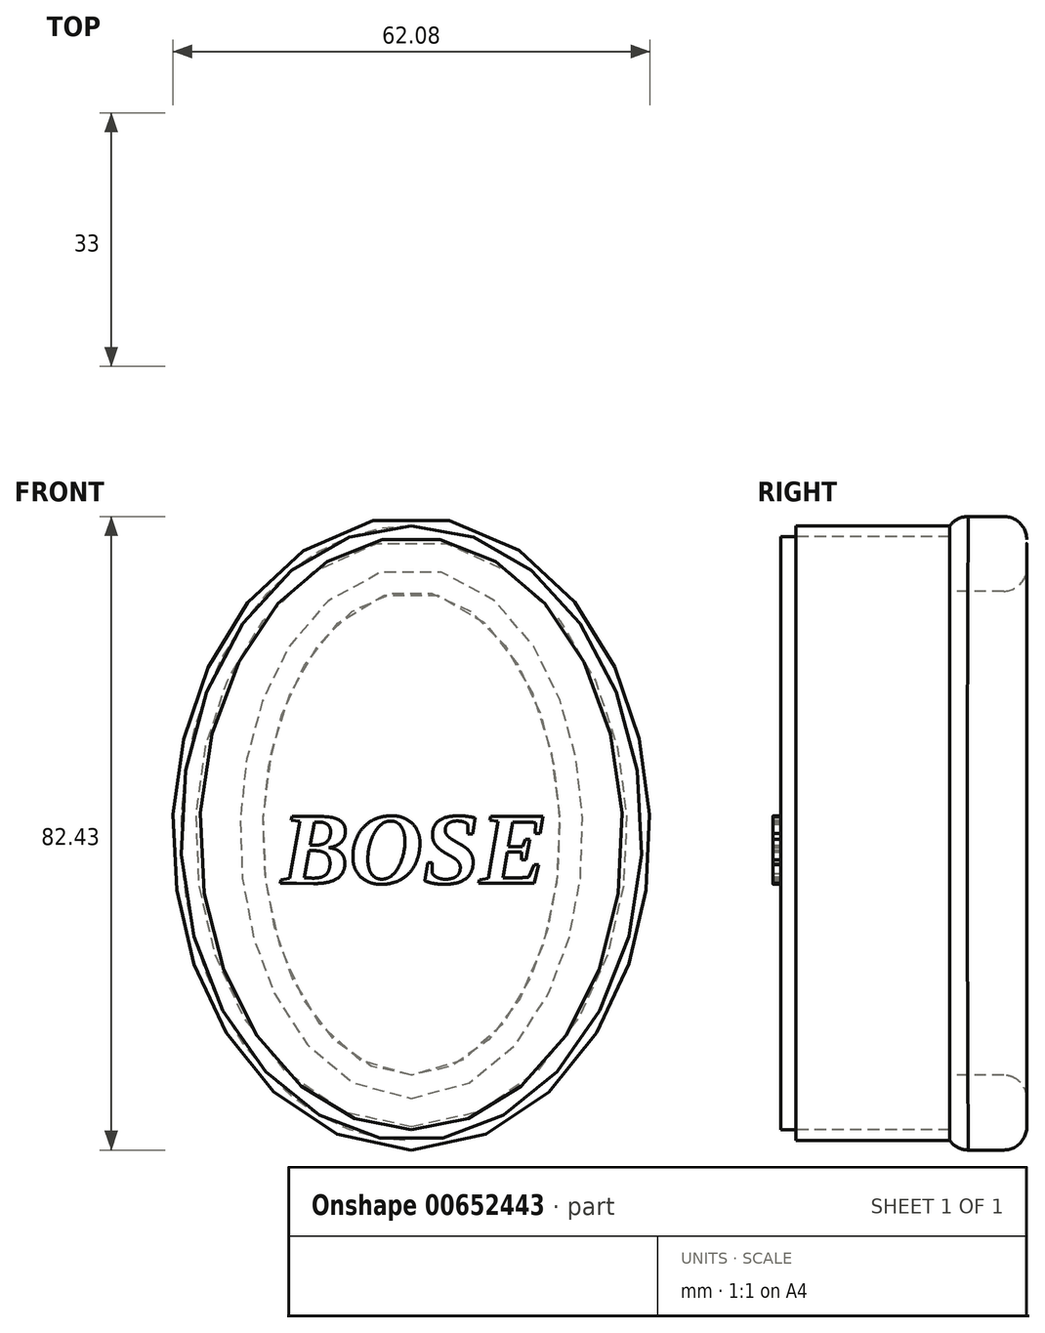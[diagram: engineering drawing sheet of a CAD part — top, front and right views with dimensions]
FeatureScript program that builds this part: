
annotation { "Feature Type Name" : "Feature", "Feature Type Description" : "" }
export const myFeature = defineFeature(function(context is Context, id is Id, definition is map)
    precondition{}
    {
        {
            var Q0;
            Q0=qCreatedBy(makeId("Front.planeOp"),FACE);
            var sketch = newSketch(context, id + "F0", { "sketchPlane" : qUnion([Q0])});
            skEllipse(sketch, "E0", {"center": v(0, 51.76) * mm, "majorRadius": 38.55 * mm, "minorRadius": 27.5 * mm, "majorAxis": v(0, -1)});
            skEllipse(sketch, "E1", {"center": v(0, 51.76) * mm, "majorRadius": 40 * mm, "minorRadius": 30 * mm, "majorAxis": v(0, 1)});
            skSolve(sketch);
        }
        {
            var Q0;
            Q0=makeQuery(id+"F0.imprint","IMPRINT",FACE,{"disambiguationData":[TD([[makeQuery(id+"F0.imprint","IMPRINT",EDGE,{"derivedFrom":sQuery(id+"F0.wireOp",EDGE,"E0")}),1.0]])]});
            extrude(context, id + "F1", {"entities" : qUnion([Q0]), "depth" : 2 * mm, "offsetDistance" : 25 * mm});
        }
        {
            var Q0;
            Q0=makeQuery(id+"F0.imprint","IMPRINT",FACE,{"disambiguationData":[TD([[makeQuery(id+"F0.imprint","IMPRINT",EDGE,{"derivedFrom":sQuery(id+"F0.wireOp",EDGE,"E0")}),-1.0]])]});
            extrude(context, id + "F2", {"entities" : qUnion([Q0]), "depth" : -20 * mm, "offsetDistance" : 25 * mm});
        }
        {
            var Q0;
            Q0=makeQuery(id+"F1.opExtrude","CAP_FACE",FACE,{"disambiguationData":[OSD([sQuery(id+"F0.wireOp",EDGE,"E0")])],"isStart":false});
            var sketch = newSketch(context, id + "F3", { "sketchPlane" : qUnion([Q0])});
            skText(sketch, "E2", { "text": "BOSE", "fontName": "Tinos-BoldItalic.ttf"});
            const initialGuessF3  = {"E2": [-0.01694, 0.04525, 1, 0, 0.00955]};
            skSetInitialGuess(sketch, initialGuessF3);
            skSolve(sketch);
        }
        {
            var Q0;
            Q0 = qSketchRegion(id + "F3", true);
            extrude(context, id + "F4", {"entities" : qUnion([Q0]), "operationType" : NewBodyOperationType.ADD, "depth" : 1 * mm, "offsetDistance" : 25 * mm});
        }
        {
            var Q0;
            Q0=makeQuery(id+"F2.opExtrude","CAP_FACE",FACE,{"disambiguationData":[OSD([sQuery(id+"F0.wireOp",EDGE,"E0"),sQuery(id+"F0.wireOp",EDGE,"E1")])],"isStart":false});
            var sketch = newSketch(context, id + "F5", { "sketchPlane" : qUnion([Q0])});
            skEllipse(sketch, "E3", {"center": v(0, 51.76) * mm, "majorRadius": 41.21 * mm, "minorRadius": 31.04 * mm, "majorAxis": v(0, -1)});
            skEllipse(sketch, "E4", {"center": v(0, 51.76) * mm, "majorRadius": 31.48 * mm, "minorRadius": 19.3 * mm, "majorAxis": v(0, -1)});
            skSolve(sketch);
        }
        {
            var Q0;
            Q0 = qSketchRegion(id + "F5", true);
            extrude(context, id + "F6", {"entities" : qUnion([Q0]), "operationType" : NewBodyOperationType.ADD, "depth" : 10 * mm, "offsetDistance" : 25 * mm});
        }
        {
            var Q0;
            Q0=makeQuery(id+"F6.opExtrude","CAP_EDGE",EDGE,{"disambiguationData":[OSD([sQuery(id+"F5.wireOp",EDGE,"E3")])],"isStart":false});
            var Q1;
            Q1=makeQuery(id+"F6.opExtrude","CAP_EDGE",EDGE,{"disambiguationData":[OSD([sQuery(id+"F5.wireOp",EDGE,"E4")])],"isStart":false});
            var Q2;
            Q2=makeQuery(id+"F6.opExtrude","CAP_EDGE",EDGE,{"disambiguationData":[OSD([sQuery(id+"F5.wireOp",EDGE,"E3")])],"isStart":true});
            fillet(context, id + "F7", {"entities" : qUnion([Q0, Q1, Q2]), "radius" : 3 * mm, "tangentPropagation" : true, "allowEdgeOverflow" : false});
        }
    });
